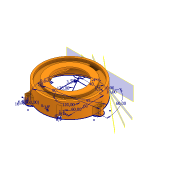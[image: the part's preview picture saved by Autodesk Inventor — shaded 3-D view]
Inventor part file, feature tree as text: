
AUTODESK INVENTOR PART (.ipt)
format: ipt  version: 2020.3 (Build 243373000, 373)  size: 384,000 bytes
history: native  units: mm
features: extrude x12, sketch x11, plane x4, revolve x1
ambient origin geometry x8: Origin, YZ Plane, XZ Plane, XY Plane, X Axis, Y Axis, Z Axis, Center Point
bodies: Body1 (feature_tree)
feature tree (28):
  sketch  "Sketch1"  dims[d0=95.0mm d1=120.0deg]
  plane  "Work Plane1"
  plane  "Work Plane2"
  plane  "Work Plane3"
  sketch  "Sketch2"  dims[d2=120.0deg d3=16.0mm]
  sketch  "Sketch3"  dims[d4=3.4mm d5=6.5mm]
  sketch  "Sketch4"  dims[d7=10.0mm d8=3.6mm]
  extrude  "Extrusion9"  TaperAngle=120.0deg  [1 undecoded]
  extrude  "Extrusion10"  Depth=16.0mm
  extrude  "Extrusion11"  Depth=6.5mm
  extrude  "Extrusion12"  Depth=10.0mm
  extrude  "Extrusion13"  Depth=1.2mm
  extrude  "Extrusion14"  Depth=9.8mm
  sketch  "Sketch5"  dims[d9=2.4mm d10=1.2mm]
  sketch  "Sketch6"  dims[d13=30.0mm d15=360.0deg d17=9.8mm]
  revolve  "Revolution1"  [1 undecoded]
  extrude  "Extrusion15"  Depth=2.0mm
  extrude  "Extrusion16"  Depth=6.1mm
  extrude  "Extrusion17"  Depth=6.1mm
  extrude  "Extrusion18"  Depth=2.5mm
  extrude  "Extrusion19"  Depth=2.5mm
  plane  "Work Plane4"
  extrude  "Extrusion20"  Depth=2.5mm
  sketch  "Sketch7"  dims[d18=12.0mm d19=2.0mm]
  sketch  "Sketch8"  dims[d20=6.0mm d21=2.0mm]
  sketch  "Sketch9"  dims[d23=60.0deg d24=6.1mm]
  sketch  "Sketch10"  dims[d25=8.0mm d26=6.1mm]
  sketch  "Sketch11"  dims[d27=60.0deg d28=1.745329mm d29=1.745329mm d46=5.5mm d47=5.5mm d48=5.5mm d56=40.0mm d57=60.0mm d58=3.2mm d59=1.3mm d60=1.0mm d61=1.0mm d62=1.3mm d64=3.0mm d65=8.0mm d66=6.0mm d74=90.0mm d75=26.0mm d76=0.0mm d77=3.0mm d78=0.0mm d79=10.0mm d80=0.0mm d81=10.0mm d82=0.0mm d83=4.2mm d84=0.0mm d85=8.4mm d86=0.0mm d87=70.0mm d88=85.0mm d89=3.5mm d90=4.0mm d91=8.5mm d92=50.5mm d93=2.0mm d94=2.0mm d95=4.0mm d96=90.0deg d97=23.5mm d98=0.0mm d99=12.5mm d100=0.0mm d101=6.5mm d102=6.0mm d103=6.0mm d104=3.0mm d105=0.0mm d106=7.25mm d107=0.0mm d108=3.490659mm d109=2.5mm d110=0.0mm d114=3.490659mm d115=4.0mm d116=4.0mm d117=90.0deg d118=5.0mm d119=2.5mm d120=12.0mm d121=0.0mm d72=0.5mm d73=0.872665mm d122=0.5mm d123=0.872665mm d124=0.5mm d125=0.872665mm]
note: 2 required parameter values undecoded (feature->parameter linkage not recoverable at this tier; creation-order binding heuristic only, values carry confidence <= 0.55)